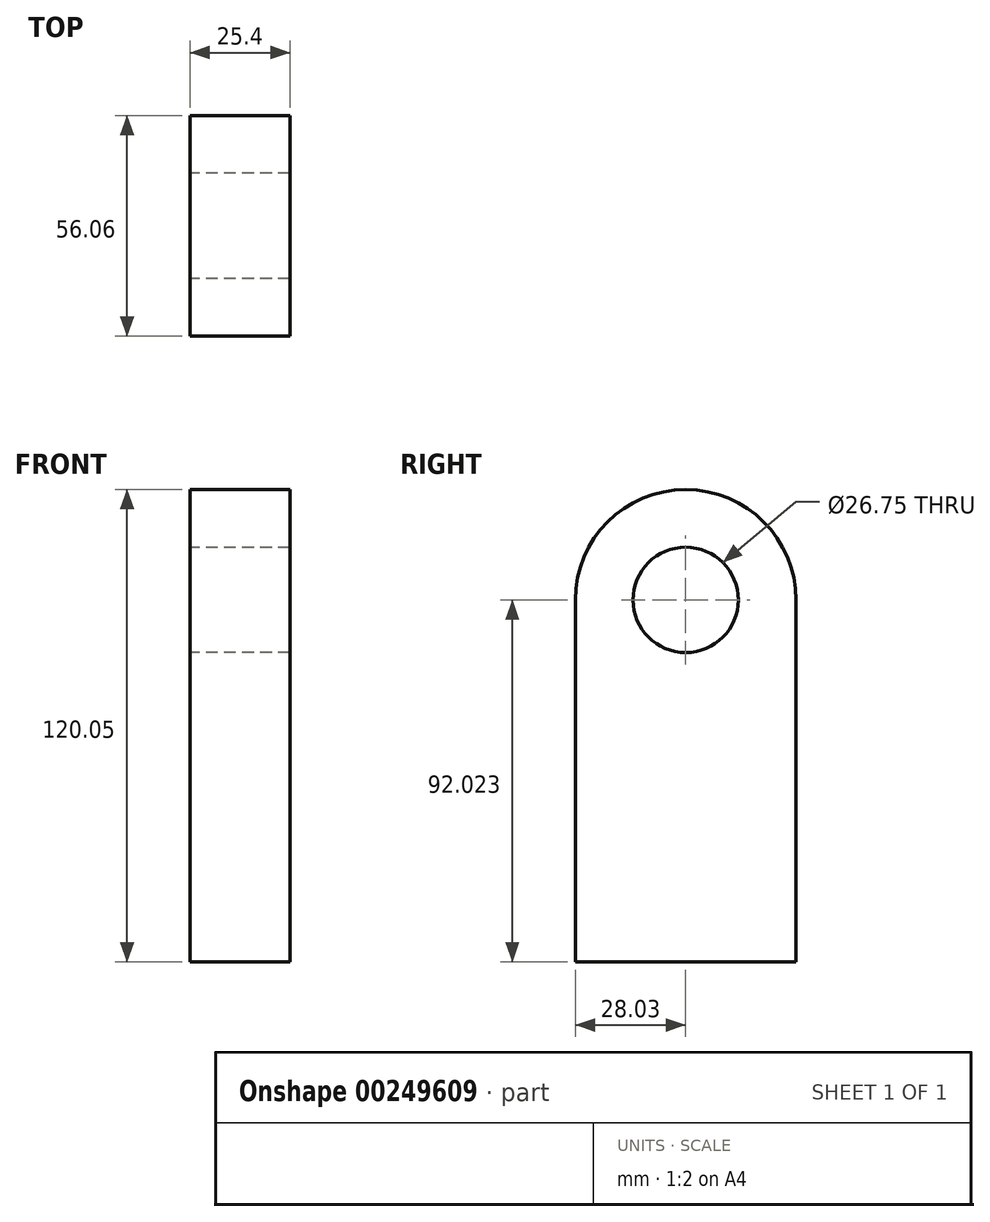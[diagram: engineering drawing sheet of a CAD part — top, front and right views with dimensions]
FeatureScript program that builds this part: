
annotation { "Feature Type Name" : "Feature", "Feature Type Description" : "" }
export const myFeature = defineFeature(function(context is Context, id is Id, definition is map)
    precondition{}
    {
        {
            var Q0;
            Q0=qCreatedBy(makeId("Right.planeOp"),FACE);
            var sketch = newSketch(context, id + "F0", { "sketchPlane" : qUnion([Q0])});
            skLineSegment(sketch, "E0.bottom", {"start": v(-13.37, 46.01) * mm, "end": v(13.37, 46.01) * mm});
            skLineSegment(sketch, "E0.top", {"start": v(-28.03, -46.01) * mm, "end": v(28.03, -46.01) * mm});
            skLineSegment(sketch, "E0.left", {"start": v(-28.03, 46.01) * mm, "end": v(-28.03, -46.01) * mm});
            skLineSegment(sketch, "E0.right", {"start": v(28.03, 46.01) * mm, "end": v(28.03, -46.01) * mm});
            skPoint(sketch, "E0.middle", {"position": v(0, 0) * mm});
            skArc(sketch, "E1", {"start": v(28.03, 46.01) * mm, "mid": v(0, 74.04) * mm, "end": v(-28.03, 46.01) * mm});
            skCircle(sketch, "E2", {"center": v(0, 46.01) * mm, "radius": 13.37 * mm});
            skSolve(sketch);
        }
        {
            var Q0;
            Q0 = qSketchRegion(id + "F0", true);
            extrude(context, id + "F1", {"entities" : qUnion([Q0]), "depth" : 25.4 * mm});
        }
    });
